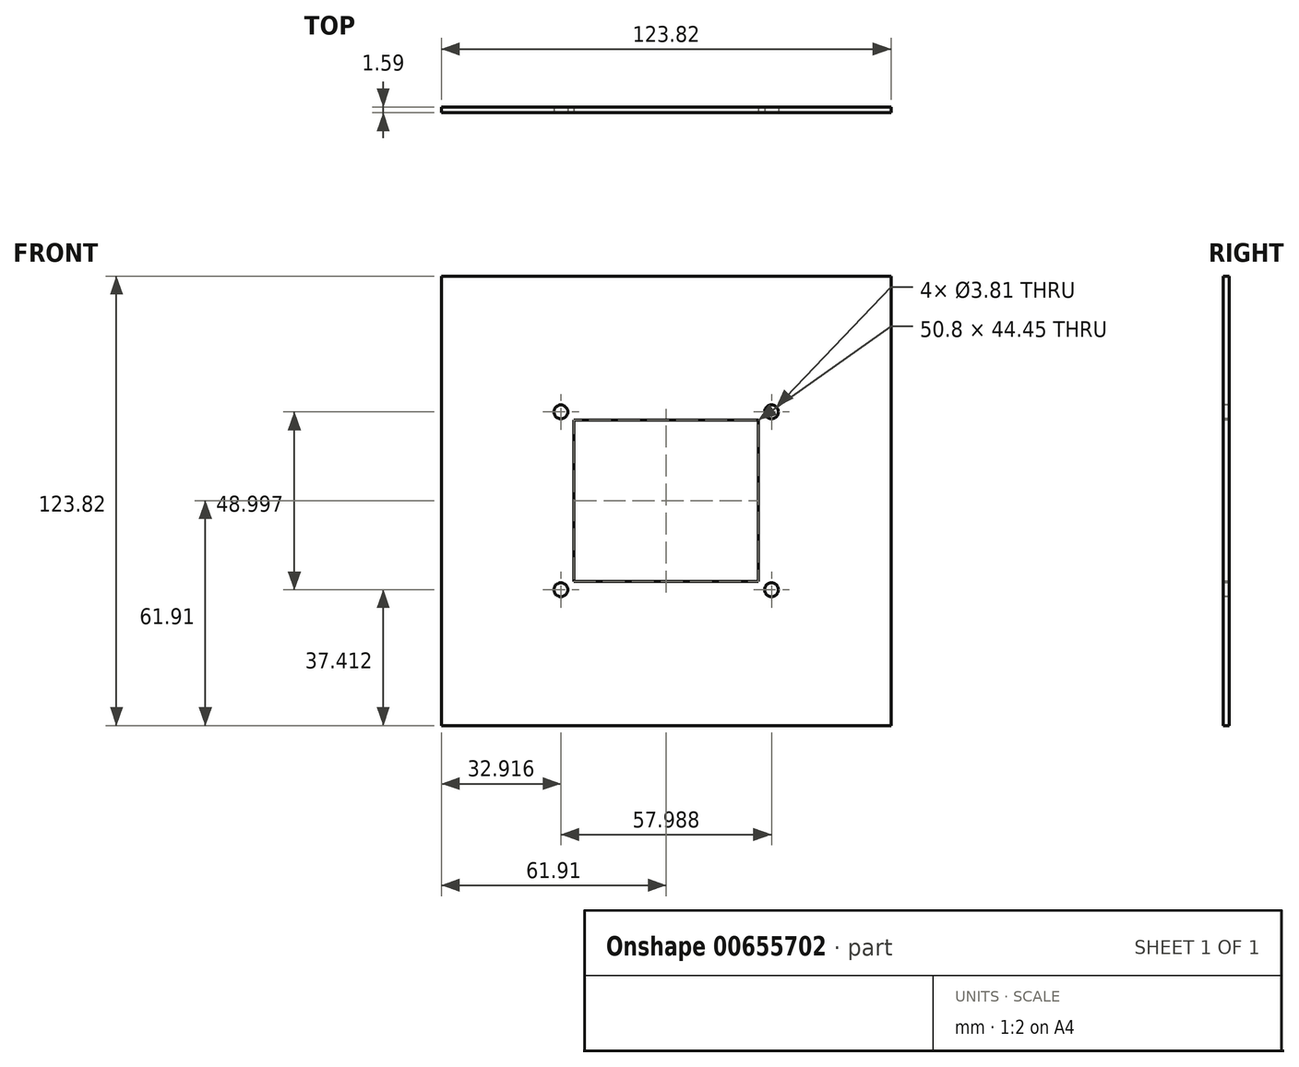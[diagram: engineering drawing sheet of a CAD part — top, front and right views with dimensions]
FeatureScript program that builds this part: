
annotation { "Feature Type Name" : "Feature", "Feature Type Description" : "" }
export const myFeature = defineFeature(function(context is Context, id is Id, definition is map)
    precondition{}
    {
        {
            var Q0;
            Q0=qCreatedBy(makeId("Front.planeOp"),FACE);
            var sketch = newSketch(context, id + "F0", { "sketchPlane" : qUnion([Q0])});
            skLineSegment(sketch, "E0.bottom", {"start": v(61.91, -61.91) * mm, "end": v(-61.91, -61.91) * mm});
            skLineSegment(sketch, "E0.top", {"start": v(61.91, 61.91) * mm, "end": v(-61.91, 61.91) * mm});
            skLineSegment(sketch, "E0.left", {"start": v(61.91, -61.91) * mm, "end": v(61.91, 61.91) * mm});
            skLineSegment(sketch, "E0.right", {"start": v(-61.91, -61.91) * mm, "end": v(-61.91, 61.91) * mm});
            skPoint(sketch, "E0.middle", {"position": v(0, 0) * mm});
            skSolve(sketch);
        }
        {
            var Q0;
            Q0 = qSketchRegion(id + "F0", true);
            extrude(context, id + "F1", {"entities" : qUnion([Q0]), "oppositeDirection" : true, "depth" : 1.59 * mm, "offsetDistance" : 25.4 * mm});
        }
        {
            var Q0;
            Q0=makeQuery(id+"F1.opExtrude","CAP_FACE",FACE,{"disambiguationData":[OSD([sQuery(id+"F0.wireOp",EDGE,"E0.bottom"),sQuery(id+"F0.wireOp",EDGE,"E0.top"),sQuery(id+"F0.wireOp",EDGE,"E0.left"),sQuery(id+"F0.wireOp",EDGE,"E0.right")])],"isStart":true});
            var sketch = newSketch(context, id + "F2", { "sketchPlane" : qUnion([Q0])});
            skLineSegment(sketch, "E1.bottom", {"start": v(29, -24.5) * mm, "end": v(-29, -24.5) * mm, "construction": true});
            skLineSegment(sketch, "E1.top", {"start": v(29, 24.5) * mm, "end": v(-29, 24.5) * mm, "construction": true});
            skLineSegment(sketch, "E1.left", {"start": v(29, -24.5) * mm, "end": v(29, 24.5) * mm, "construction": true});
            skLineSegment(sketch, "E1.right", {"start": v(-29, -24.5) * mm, "end": v(-29, 24.5) * mm, "construction": true});
            skPoint(sketch, "E1.middle", {"position": v(0, 0) * mm});
            skCircle(sketch, "E2", {"center": v(29, 24.5) * mm, "radius": 1.9 * mm});
            skCircle(sketch, "E3", {"center": v(29, -24.5) * mm, "radius": 1.9 * mm});
            skCircle(sketch, "E4", {"center": v(-29, -24.5) * mm, "radius": 1.9 * mm});
            skCircle(sketch, "E5", {"center": v(-29, 24.5) * mm, "radius": 1.9 * mm});
            skLineSegment(sketch, "E6.bottom", {"start": v(25.4, -22.23) * mm, "end": v(-25.4, -22.23) * mm});
            skLineSegment(sketch, "E6.top", {"start": v(25.4, 22.23) * mm, "end": v(-25.4, 22.22) * mm});
            skLineSegment(sketch, "E6.left", {"start": v(25.4, -22.23) * mm, "end": v(25.4, 22.23) * mm});
            skLineSegment(sketch, "E6.right", {"start": v(-25.4, -22.23) * mm, "end": v(-25.4, 22.23) * mm});
            skSolve(sketch);
        }
        {
            var Q0;
            Q0 = qSketchRegion(id + "F2", true);
            extrude(context, id + "F3", {"entities" : qUnion([Q0]), "operationType" : NewBodyOperationType.REMOVE, "oppositeDirection" : true, "depth" : 25.4 * mm, "offsetDistance" : 25.4 * mm});
        }
    });
